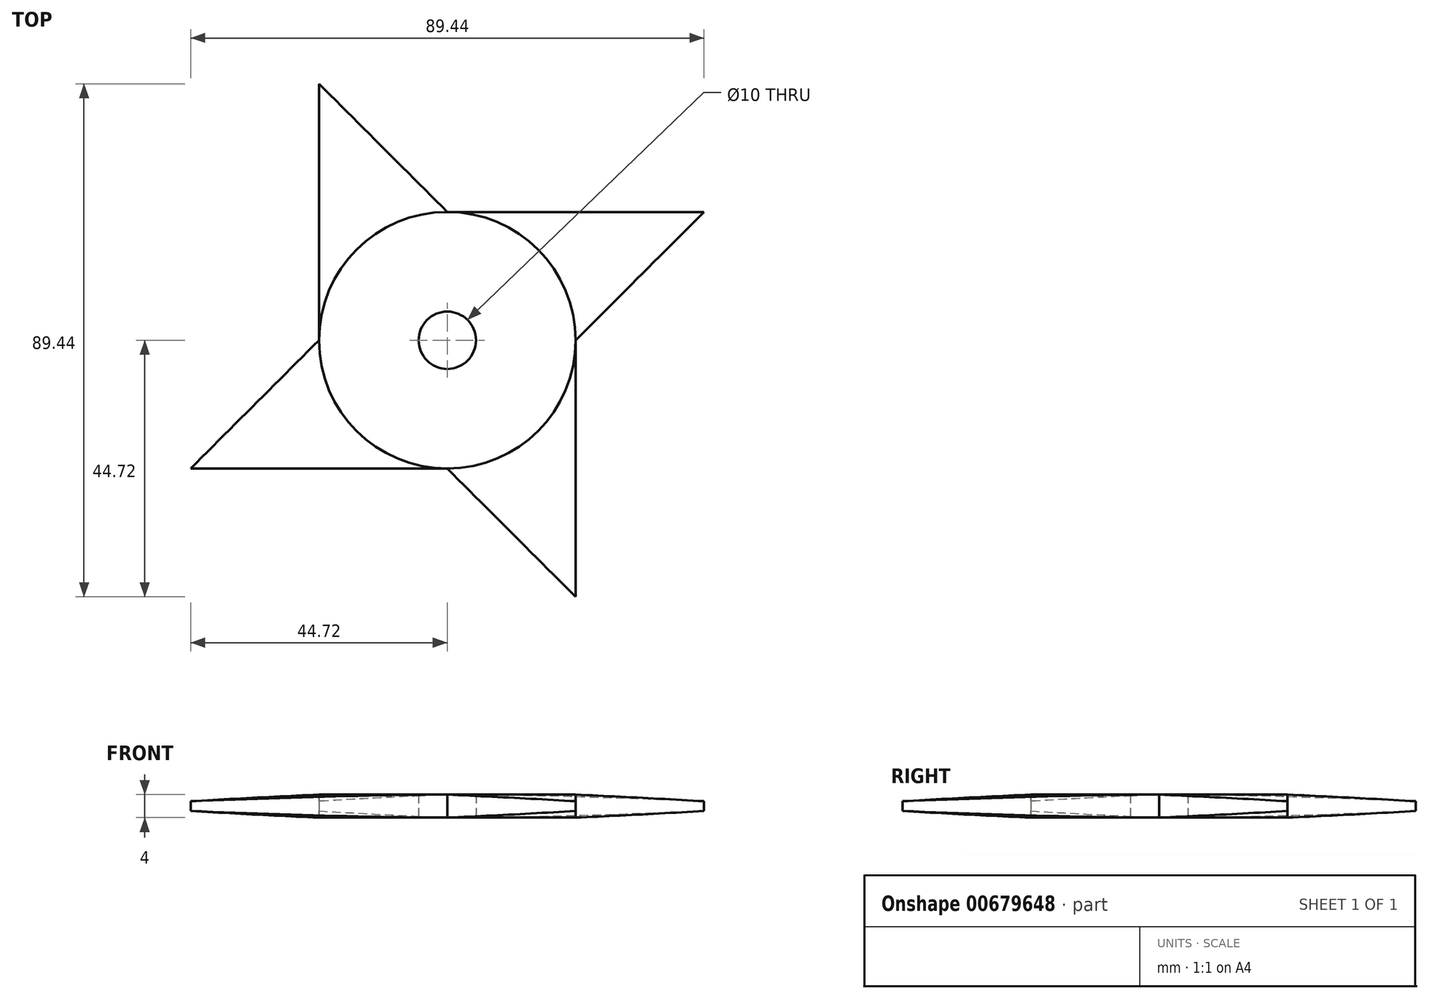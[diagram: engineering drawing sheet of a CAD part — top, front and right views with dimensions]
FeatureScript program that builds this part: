
annotation { "Feature Type Name" : "Feature", "Feature Type Description" : "" }
export const myFeature = defineFeature(function(context is Context, id is Id, definition is map)
    precondition{}
    {
        {
            var Q0;
            Q0=qCreatedBy(makeId("Top.planeOp"),FACE);
            var sketch = newSketch(context, id + "F0", { "sketchPlane" : qUnion([Q0])});
            skLineSegment(sketch, "E0.bottom", {"start": v(0, 0) * mm, "end": v(-22.36, 0) * mm});
            skLineSegment(sketch, "E0.left", {"start": v(0, 0) * mm, "end": v(0, 22.36) * mm});
            skLineSegment(sketch, "E0.right", {"start": v(-22.36, 0) * mm, "end": v(-22.36, 22.36) * mm});
            skLineSegment(sketch, "E1", {"start": v(-22.36, 22.36) * mm, "end": v(-22.36, 44.72) * mm});
            skLineSegment(sketch, "E2", {"start": v(-22.36, 44.72) * mm, "end": v(0, 22.36) * mm});
            skLineSegment(sketch, "E3.bottom", {"start": v(0, 22.36) * mm, "end": v(22.36, 22.36) * mm});
            skLineSegment(sketch, "E3.top", {"start": v(0, 0) * mm, "end": v(22.36, 0) * mm});
            skLineSegment(sketch, "E3.left", {"start": v(0, 22.36) * mm, "end": v(0, 0) * mm});
            skLineSegment(sketch, "E4.MirrorCS", {"start": v(0, -22.36) * mm, "end": v(0, 0) * mm});
            skLineSegment(sketch, "E5.MirrorCS", {"start": v(0, -22.36) * mm, "end": v(-22.36, -22.36) * mm});
            skLineSegment(sketch, "E6.MirrorCS", {"start": v(22.36, -22.36) * mm, "end": v(22.36, 0) * mm});
            skLineSegment(sketch, "E7", {"start": v(22.36, 22.36) * mm, "end": v(44.72, 22.36) * mm});
            skLineSegment(sketch, "E8", {"start": v(44.72, 22.36) * mm, "end": v(22.36, 0) * mm});
            skLineSegment(sketch, "E9", {"start": v(22.36, -22.36) * mm, "end": v(22.36, -44.72) * mm});
            skLineSegment(sketch, "E10", {"start": v(22.36, -44.72) * mm, "end": v(0, -22.36) * mm});
            skLineSegment(sketch, "E11", {"start": v(-22.36, -22.36) * mm, "end": v(-44.72, -22.36) * mm});
            skLineSegment(sketch, "E12", {"start": v(-44.72, -22.36) * mm, "end": v(-22.36, 0) * mm});
            skCircle(sketch, "E13", {"center": v(0, 0) * mm, "radius": 5 * mm});
            skSolve(sketch);
        }
        {
            var Q0;
            {var subQ1=sQuery(id+"F0.wireOp",EDGE,"E3.bottom");Q0=makeQuery(id+"F0.imprint","IMPRINT",FACE,{"disambiguationData":[TD([[makeQuery(id+"F0.imprint","IMPRINT",EDGE,{"derivedFrom":subQ1}),-1.0]])]});}
            var Q1;
            {var subQ1=sQuery(id+"F0.wireOp",EDGE,"E0.right");Q1=makeQuery(id+"F0.imprint","IMPRINT",FACE,{"disambiguationData":[TD([[makeQuery(id+"F0.imprint","IMPRINT",EDGE,{"derivedFrom":subQ1}),-1.0]])]});}
            var Q2;
            {var subQ0=sQuery(id+"F0.wireOp",EDGE,"E5.MirrorCS");Q2=makeQuery(id+"F0.imprint","IMPRINT",FACE,{"disambiguationData":[TD([[makeQuery(id+"F0.imprint","IMPRINT",EDGE,{"derivedFrom":subQ0}),-1.0]])]});}
            var Q3;
            {var subQ0=sQuery(id+"F0.wireOp",EDGE,"E6.MirrorCS");Q3=makeQuery(id+"F0.imprint","IMPRINT",FACE,{"disambiguationData":[TD([[makeQuery(id+"F0.imprint","IMPRINT",EDGE,{"derivedFrom":subQ0}),1.0]])]});}
            extrude(context, id + "F1", {"entities" : qUnion([Q0, Q1, Q2, Q3]), "endBound" : BoundingType.SYMMETRIC, "depth" : 4 * mm, "offsetDistance" : 25.4 * mm});
        }
        {
            var Q0;
            Q0=qCreatedBy(makeId("Right.planeOp"),FACE);
            var sketch = newSketch(context, id + "F2", { "sketchPlane" : qUnion([Q0])});
            skLineSegment(sketch, "E14", {"start": v(-22.36, 2) * mm, "end": v(-70.62, 2) * mm});
            skLineSegment(sketch, "E15", {"start": v(-70.62, 2) * mm, "end": v(-70.62, -2) * mm});
            skLineSegment(sketch, "E16", {"start": v(-70.62, -2) * mm, "end": v(-22.36, -2) * mm});
            skLineSegment(sketch, "E17", {"start": v(-22.36, -2) * mm, "end": v(-22.36, 2) * mm});
            skLineSegment(sketch, "E18", {"start": v(-70.62, 0) * mm, "end": v(-22.36, 2) * mm});
            skLineSegment(sketch, "E19", {"start": v(-22.36, -2) * mm, "end": v(-70.62, 0) * mm});
            skSolve(sketch);
        }
        {
            var Q0;
            {var subQ0=sQuery(id+"F2.wireOp",EDGE,"E14");Q0=makeQuery(id+"F2.imprint","IMPRINT",FACE,{"disambiguationData":[TD([[makeQuery(id+"F2.imprint","IMPRINT",EDGE,{"derivedFrom":subQ0}),1.0]])]});}
            var Q1;
            {var subQ0=sQuery(id+"F2.wireOp",EDGE,"E16");Q1=makeQuery(id+"F2.imprint","IMPRINT",FACE,{"disambiguationData":[TD([[makeQuery(id+"F2.imprint","IMPRINT",EDGE,{"derivedFrom":subQ0}),1.0]])]});}
            var Q2;
            Q2=makeQuery(id+"F1.opExtrude","CAP_EDGE",EDGE,{"disambiguationData":[OSD([sQuery(id+"F0.wireOp",EDGE,"E13")])],"isStart":false});
            revolve(context, id + "F3", {"operationType" : NewBodyOperationType.REMOVE, "entities" : qUnion([Q0, Q1]), "axis" : qUnion([Q2]), "revolveType" : RevolveType.FULL, "oppositeDirection" : true});
        }
    });
